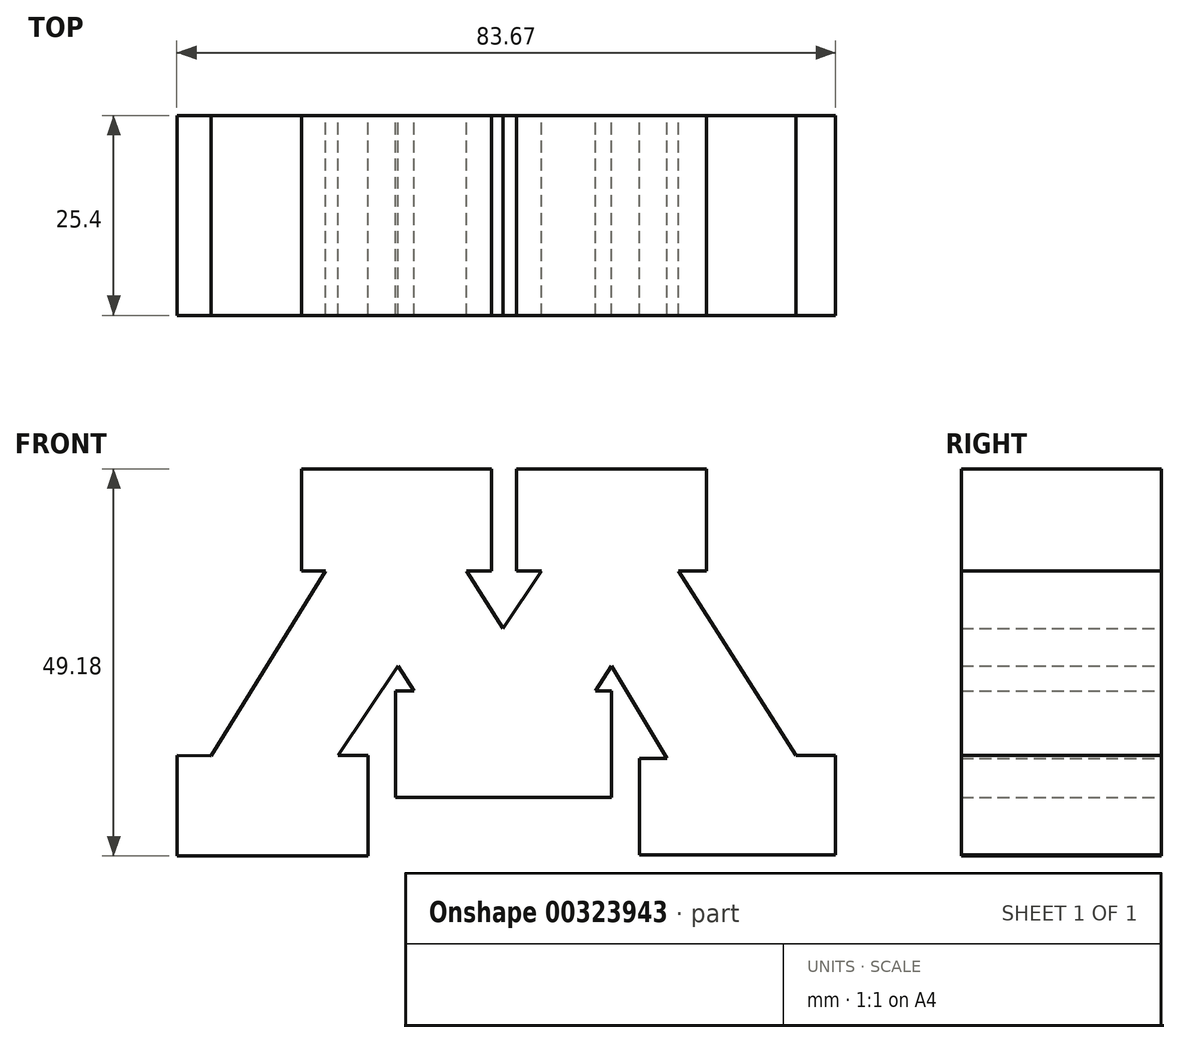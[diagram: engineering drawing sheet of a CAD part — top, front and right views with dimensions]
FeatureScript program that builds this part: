
annotation { "Feature Type Name" : "Feature", "Feature Type Description" : "" }
export const myFeature = defineFeature(function(context is Context, id is Id, definition is map)
    precondition{}
    {
        {
            var Q0;
            Q0=qCreatedBy(makeId("Front.planeOp"),FACE);
            var sketch = newSketch(context, id + "F0", { "sketchPlane" : qUnion([Q0])});
            skFitSpline(sketch, "E0", {"points": [v(-33.72, 5.28) * mm, v(-19.19, 28.78) * mm], "startDerivative": vector(14.53, 23.5) * mm, "endDerivative": vector(14.53, 23.5) * mm});
            skFitSpline(sketch, "E1", {"points": [v(-19.19, 28.78) * mm, v(-22.23, 28.78) * mm], "startDerivative": vector(-3.04, 0) * mm, "endDerivative": vector(-3.04, 0) * mm});
            skFitSpline(sketch, "E2", {"points": [v(-22.23, 28.78) * mm, v(-22.23, 41.73) * mm], "startDerivative": vector(0, 12.95) * mm, "endDerivative": vector(0, 12.95) * mm});
            skFitSpline(sketch, "E3", {"points": [v(-22.23, 41.73) * mm, v(1.9, 41.73) * mm], "startDerivative": vector(24.13, 0) * mm, "endDerivative": vector(24.13, 0) * mm});
            skFitSpline(sketch, "E4", {"points": [v(1.9, 41.73) * mm, v(1.9, 28.78) * mm], "startDerivative": vector(0, -12.95) * mm, "endDerivative": vector(0, -12.95) * mm});
            skFitSpline(sketch, "E5", {"points": [v(1.9, 28.78) * mm, v(-1.29, 28.78) * mm], "startDerivative": vector(-3.19, 0) * mm, "endDerivative": vector(-3.19, 0) * mm});
            skFitSpline(sketch, "E6", {"points": [v(-1.29, 28.78) * mm, v(3.38, 21.47) * mm], "startDerivative": vector(4.67, -7.31) * mm, "endDerivative": vector(4.67, -7.31) * mm});
            skFitSpline(sketch, "E7", {"points": [v(3.38, 21.47) * mm, v(8.27, 28.78) * mm], "startDerivative": vector(4.9, 7.31) * mm, "endDerivative": vector(4.9, 7.31) * mm});
            skLineSegment(sketch, "E8", {"start": v(8.27, 28.78) * mm, "end": v(5.09, 28.78) * mm});
            skLineSegment(sketch, "E9", {"start": v(5.09, 28.78) * mm, "end": v(5.09, 41.73) * mm});
            skLineSegment(sketch, "E10", {"start": v(5.09, 41.73) * mm, "end": v(29.22, 41.73) * mm});
            skLineSegment(sketch, "E11", {"start": v(29.22, 41.73) * mm, "end": v(29.22, 28.78) * mm});
            skLineSegment(sketch, "E12", {"start": v(29.22, 28.78) * mm, "end": v(25.69, 28.78) * mm});
            skLineSegment(sketch, "E13", {"start": v(25.69, 28.78) * mm, "end": v(40.6, 5.3) * mm});
            skLineSegment(sketch, "E14", {"start": v(40.6, 5.3) * mm, "end": v(45.6, 5.3) * mm});
            skLineSegment(sketch, "E15", {"start": v(45.6, 5.3) * mm, "end": v(45.6, -7.33) * mm});
            skLineSegment(sketch, "E16", {"start": v(45.6, -7.33) * mm, "end": v(20.68, -7.33) * mm});
            skLineSegment(sketch, "E17", {"start": v(20.68, -7.33) * mm, "end": v(20.68, 4.96) * mm});
            skLineSegment(sketch, "E18", {"start": v(20.68, 4.96) * mm, "end": v(24.2, 4.96) * mm});
            skLineSegment(sketch, "E19", {"start": v(24.2, 4.96) * mm, "end": v(17.15, 16.69) * mm});
            skLineSegment(sketch, "E20", {"start": v(17.15, 16.69) * mm, "end": v(15.1, 13.5) * mm});
            skLineSegment(sketch, "E21", {"start": v(17.15, 13.5) * mm, "end": v(17.15, 0) * mm});
            skLineSegment(sketch, "E22", {"start": v(17.15, 0) * mm, "end": v(-10.28, 0) * mm});
            skLineSegment(sketch, "E23", {"start": v(17.15, 13.5) * mm, "end": v(15.1, 13.5) * mm});
            skLineSegment(sketch, "E24", {"start": v(-10.28, 0) * mm, "end": v(-10.28, 13.5) * mm});
            skLineSegment(sketch, "E25", {"start": v(-10.28, 13.5) * mm, "end": v(-7.91, 13.5) * mm});
            skLineSegment(sketch, "E26", {"start": v(-7.91, 13.5) * mm, "end": v(-9.94, 16.69) * mm});
            skLineSegment(sketch, "E27", {"start": v(-9.94, 16.69) * mm, "end": v(-17.57, 5.3) * mm});
            skLineSegment(sketch, "E28", {"start": v(-17.57, 5.3) * mm, "end": v(-13.75, 5.3) * mm});
            skPoint(sketch, "E28.endSnap0", {"position": v(-13.75, 11) * mm});
            skLineSegment(sketch, "E29", {"start": v(-13.75, 5.3) * mm, "end": v(-13.75, -7.45) * mm});
            skLineSegment(sketch, "E30", {"start": v(-13.75, -7.45) * mm, "end": v(-38.06, -7.45) * mm});
            skLineSegment(sketch, "E31", {"start": v(-38.06, -7.45) * mm, "end": v(-38.06, 5.3) * mm});
            skLineSegment(sketch, "E32", {"start": v(-38.06, 5.3) * mm, "end": v(-33.72, 5.28) * mm});
            skSolve(sketch);
        }
        {
            var Q0;
            Q0=makeQuery(id+"F0.imprint","IMPRINT",FACE,{"disambiguationData":[TD([[makeQuery(id+"F0.imprint","IMPRINT",EDGE,{"derivedFrom":sQuery(id+"F0.wireOp",EDGE,"E0")}),-1.0]])]});
            extrude(context, id + "F1", {"entities" : qUnion([Q0]), "depth" : 25.4 * mm});
        }
    });
